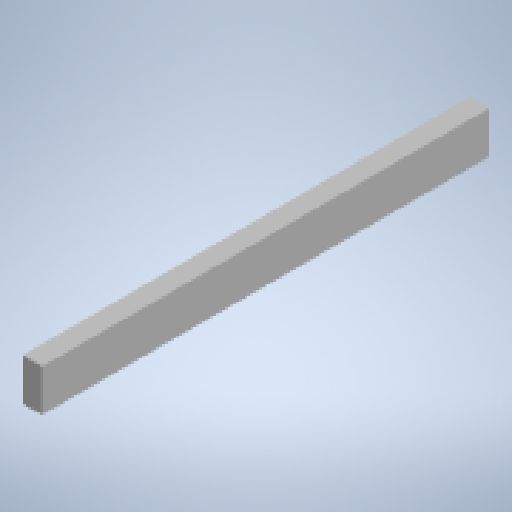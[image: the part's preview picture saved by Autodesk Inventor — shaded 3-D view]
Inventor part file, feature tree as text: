
AUTODESK INVENTOR PART (.ipt)
format: ipt  version: 2023 (Build 270158000, 158)  size: 128,000 bytes
history: native  units: in
note: dims shown in document units (in); Inventor stores cm internally (conversion verified against a paired STEP export)
features: extrude x1, sketch x1
ambient origin geometry x8: Origin, YZ Plane, XZ Plane, XY Plane, X Axis, Y Axis, Z Axis, Center Point
bodies: Solid1 (feature_tree)
feature tree (2):
  extrude  "Extrusion1"  Depth=1.75in
  sketch  "Sketch1"  dims[d0=3.75in d1=1.75in d2=40.0in d3=0.0in]
